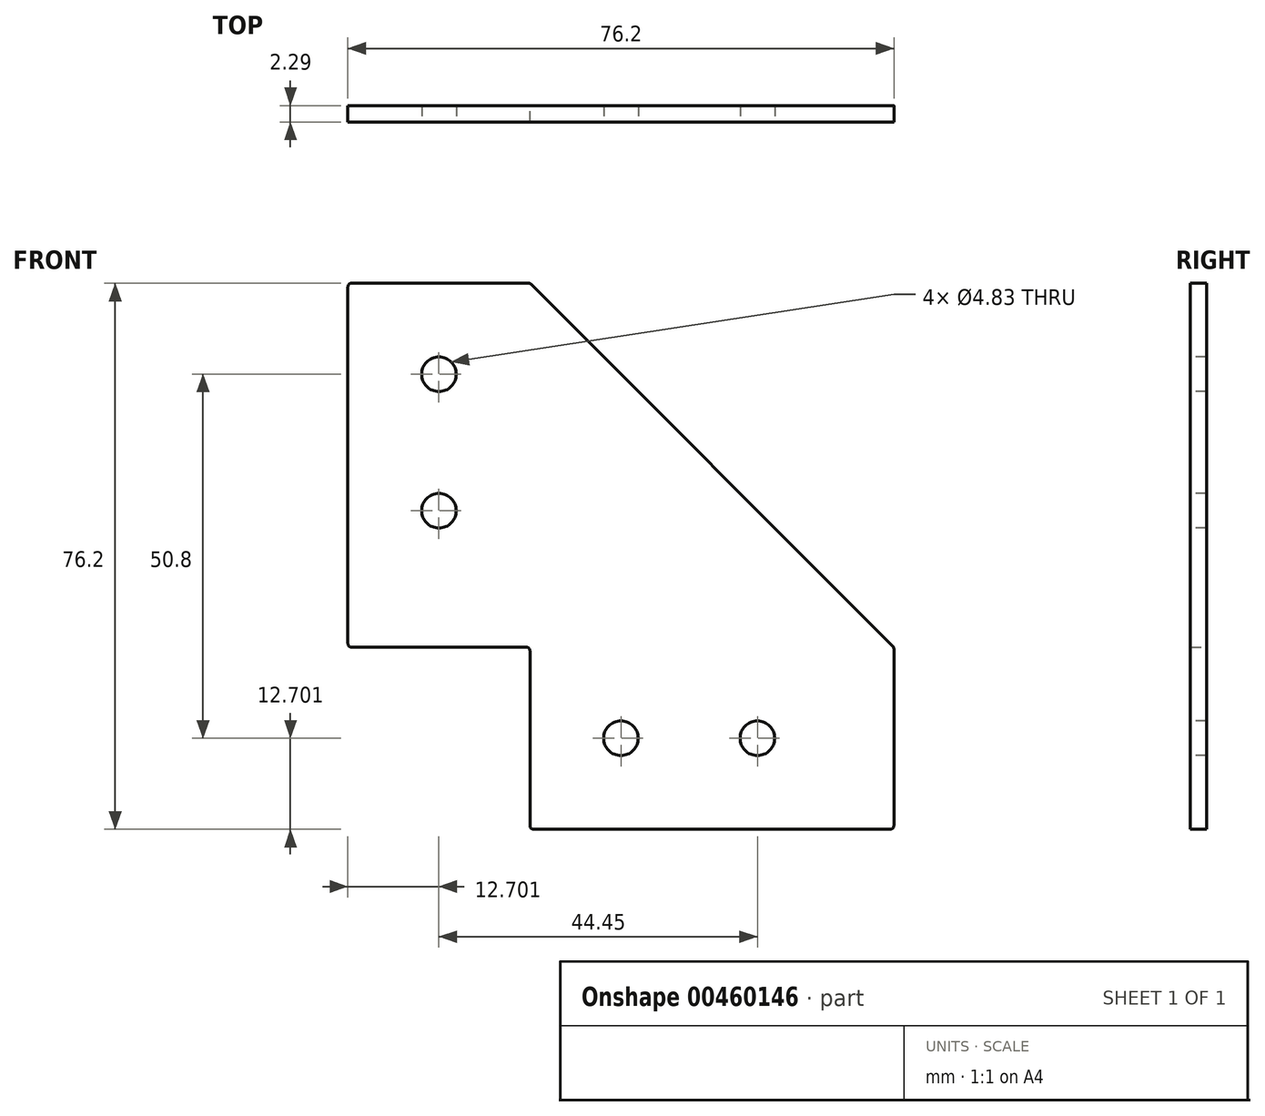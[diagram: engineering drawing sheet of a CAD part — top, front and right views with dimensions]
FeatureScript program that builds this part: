
annotation { "Feature Type Name" : "Feature", "Feature Type Description" : "" }
export const myFeature = defineFeature(function(context is Context, id is Id, definition is map)
    precondition{}
    {
        {
            var Q0;
            Q0=qCreatedBy(makeId("Front.planeOp"),FACE);
            var sketch = newSketch(context, id + "F0", { "sketchPlane" : qUnion([Q0])});
            skLineSegment(sketch, "E0", {"start": v(-40.26, 44.23) * mm, "end": v(-40.26, -6.57) * mm});
            skLineSegment(sketch, "E1", {"start": v(-40.26, -6.57) * mm, "end": v(-14.86, -6.57) * mm});
            skLineSegment(sketch, "E2", {"start": v(-14.86, -6.57) * mm, "end": v(-14.86, -31.97) * mm});
            skLineSegment(sketch, "E3", {"start": v(-14.86, -31.97) * mm, "end": v(35.94, -31.97) * mm});
            skLineSegment(sketch, "E4", {"start": v(35.94, -31.97) * mm, "end": v(35.94, -6.57) * mm});
            skLineSegment(sketch, "E5", {"start": v(-40.26, 44.23) * mm, "end": v(-14.86, 44.23) * mm});
            skLineSegment(sketch, "E6", {"start": v(-14.86, 44.23) * mm, "end": v(35.94, -6.57) * mm});
            skLineSegment(sketch, "E7", {"start": v(-14.86, 44.23) * mm, "end": v(-14.86, -6.57) * mm, "construction": true});
            skLineSegment(sketch, "E8", {"start": v(35.94, -6.57) * mm, "end": v(-14.86, -6.57) * mm, "construction": true});
            skSolve(sketch);
        }
        {
            var Q0;
            Q0=makeQuery(id+"F0.imprint","IMPRINT",FACE,{"disambiguationData":[TD([[makeQuery(id+"F0.imprint","IMPRINT",EDGE,{"derivedFrom":sQuery(id+"F0.wireOp",EDGE,"E0")}),1.0]])]});
            extrude(context, id + "F1", {"entities" : qUnion([Q0]), "depth" : 2.3 * mm});
        }
        {
            var Q0;
            Q0=makeQuery(id+"F1.opExtrude","CAP_FACE",FACE,{"disambiguationData":[OSD([sQuery(id+"F0.wireOp",EDGE,"E0"),sQuery(id+"F0.wireOp",EDGE,"E1"),sQuery(id+"F0.wireOp",EDGE,"E2"),sQuery(id+"F0.wireOp",EDGE,"E3"),sQuery(id+"F0.wireOp",EDGE,"E4"),sQuery(id+"F0.wireOp",EDGE,"E5"),sQuery(id+"F0.wireOp",EDGE,"E6")])],"isStart":false});
            var sketch = newSketch(context, id + "F2", { "sketchPlane" : qUnion([Q0])});
            skCircle(sketch, "E9", {"center": v(-27.56, 31.53) * mm, "radius": 2.41 * mm});
            skCircle(sketch, "E10", {"center": v(-27.56, 12.48) * mm, "radius": 2.41 * mm});
            skCircle(sketch, "E11", {"center": v(16.9, -19.27) * mm, "radius": 2.41 * mm});
            skCircle(sketch, "E12", {"center": v(-2.16, -19.27) * mm, "radius": 2.41 * mm});
            skSolve(sketch);
        }
        {
            var Q0;
            Q0=makeQuery(id+"F2.imprint","IMPRINT",FACE,{"disambiguationData":[TD([[makeQuery(id+"F2.imprint","IMPRINT",EDGE,{"derivedFrom":sQuery(id+"F2.wireOp",EDGE,"E9")}),1.0]])]});
            var Q1;
            Q1=makeQuery(id+"F2.imprint","IMPRINT",FACE,{"disambiguationData":[TD([[makeQuery(id+"F2.imprint","IMPRINT",EDGE,{"derivedFrom":sQuery(id+"F2.wireOp",EDGE,"E10")}),1.0]])]});
            var Q2;
            Q2=makeQuery(id+"F2.imprint","IMPRINT",FACE,{"disambiguationData":[TD([[makeQuery(id+"F2.imprint","IMPRINT",EDGE,{"derivedFrom":sQuery(id+"F2.wireOp",EDGE,"E12")}),1.0]])]});
            var Q3;
            Q3=makeQuery(id+"F2.imprint","IMPRINT",FACE,{"disambiguationData":[TD([[makeQuery(id+"F2.imprint","IMPRINT",EDGE,{"derivedFrom":sQuery(id+"F2.wireOp",EDGE,"E11")}),1.0]])]});
            extrude(context, id + "F3", {"entities" : qUnion([Q0, Q1, Q2, Q3]), "operationType" : NewBodyOperationType.REMOVE, "oppositeDirection" : true, "depth" : 2.3 * mm});
        }
        {
            var Q0;
            Q0=makeQuery(id+"F1.opExtrude","SWEPT_EDGE",EDGE,{"disambiguationData":[OSD([sQuery(id+"F0.wireOp",EDGE,"E0"),sQuery(id+"F0.wireOp",EDGE,"E5")])]});
            var Q1;
            Q1=makeQuery(id+"F1.opExtrude","SWEPT_EDGE",EDGE,{"disambiguationData":[OSD([sQuery(id+"F0.wireOp",EDGE,"E0"),sQuery(id+"F0.wireOp",EDGE,"E1")])]});
            var Q2;
            Q2=makeQuery(id+"F1.opExtrude","SWEPT_EDGE",EDGE,{"disambiguationData":[OSD([sQuery(id+"F0.wireOp",EDGE,"E2"),sQuery(id+"F0.wireOp",EDGE,"E3")])]});
            var Q3;
            Q3=makeQuery(id+"F1.opExtrude","SWEPT_EDGE",EDGE,{"disambiguationData":[OSD([sQuery(id+"F0.wireOp",EDGE,"E1"),sQuery(id+"F0.wireOp",EDGE,"E2")])]});
            var Q4;
            Q4=makeQuery(id+"F1.opExtrude","SWEPT_EDGE",EDGE,{"disambiguationData":[OSD([sQuery(id+"F0.wireOp",EDGE,"E3"),sQuery(id+"F0.wireOp",EDGE,"E4")])]});
            var Q5;
            Q5=makeQuery(id+"F1.opExtrude","SWEPT_EDGE",EDGE,{"disambiguationData":[OSD([sQuery(id+"F0.wireOp",EDGE,"E4"),sQuery(id+"F0.wireOp",EDGE,"E6")])]});
            var Q6;
            Q6=makeQuery(id+"F1.opExtrude","SWEPT_EDGE",EDGE,{"disambiguationData":[OSD([sQuery(id+"F0.wireOp",EDGE,"E5"),sQuery(id+"F0.wireOp",EDGE,"E6")])]});
            fillet(context, id + "F4", {"entities" : qUnion([Q0, Q1, Q2, Q3, Q4, Q5, Q6]), "radius" : 0.5 * mm, "tangentPropagation" : true, "allowEdgeOverflow" : false});
        }
    });
